# Revit family: Тактильная полиуретановая плитка шахматный порядок (приклеивание)
name_source: partatom
category: Оборудование
revit_build: Autodesk Revit 2017 (Build: 20160225_1515(x64)
units: mm (PartAtom-declared; Revit-internal decimal feet)

## family parameters
Общий = Да
Основа = Грань
При загрузке вырезать с полостями = Да
Размер круглого соединителя = Использовать диаметр
Тип детали = Нормальный
Точка расчета площади = Нет

## types (2) — shared parameters
ADSK_Наименование = Тактильная плитка полиуретан рифы в шахматном порядке (приклеивание)
ADSK_Размер_Высота рифа = 5 мм
ADSK_Размер_Габариты = 300Х300
ADSK_Размер_Длина = 300 мм
ADSK_Размер_Толщина = 2 мм
ADSK_Размер_Ширина = 300 мм
ADSK_Тип рифов = Тактильные конусообразные рифы в шахматном порядке
URL = http://tiflocentre.ru
Изготовитель = ТИФЛОЦЕНТР «ВЕРТИКАЛЬ»
Применение = Улица/Помещение
Стоимость = 378 $
zero-valued in all types: Отметка по умолчанию

## per-type parameters (varying)
| type | ADSK_Код изделия | ADSK_Материал наименование | ADSK_Материал плитки | Описание |
| Тактильная полиуретановая плитка_Желтая | 10129-ZH | Полиуретан, цвет желтый | Вертикаль_Полиуретан_Желтый | Тактильная полиуретановая (ПУ) плитка от компании "Вертикаль" предназначена для обеспечения информирования при движении людей с ограничениями зрения. В зависимости от взаимного расположения несет различную тактильную информацию. В данном случае желтая ПУ плитка имеет на поверхности выпуклые рифы, расположенные в шахматном порядке. Такое расположение рифов информирует человека о зонах повышенной опасности и о преградах на пути следования. Желтый цвет тактильной плитки создает контрастный эффект к темной поверхности. Тактильная ПУ плитка от Тифлоцентра "Вертикаль" монтируется при помощи клея. Мы рекомендуем использовать специальный клей |
| Тактильная полиуретановая плитка_Черная | 10129-CH | Полиуретан, цвет черный | Вертикаль_Полиуретан_Черный | Тактильная ПУ плитка предназначена для обеспечения информирования при движении тотально слепого и  слабовидящего человека. Тактильная плитка с конусообразынми рифами в шахматном порядке применяется в зонах внимания и перед преградами, которые невозможно преодолеть (столб, мебель). Черный цвет плитки является отличным контрастом к светлой поверхности (например, кафельный или мраморный пол светлого цвета), что особенно важно для слабовидящих людей. Тактильная ПУ плитка является универсальной: ее можно монтировать как в помещении, так и на улице прямо на асфальт. Тактильная ПУ плитка монтируется при помощи специального клея FIXVERT. Тактильная плитка от компании "Вертикаль" рекомендована к применению ВОС и гос. программой "Доступная среда" |
